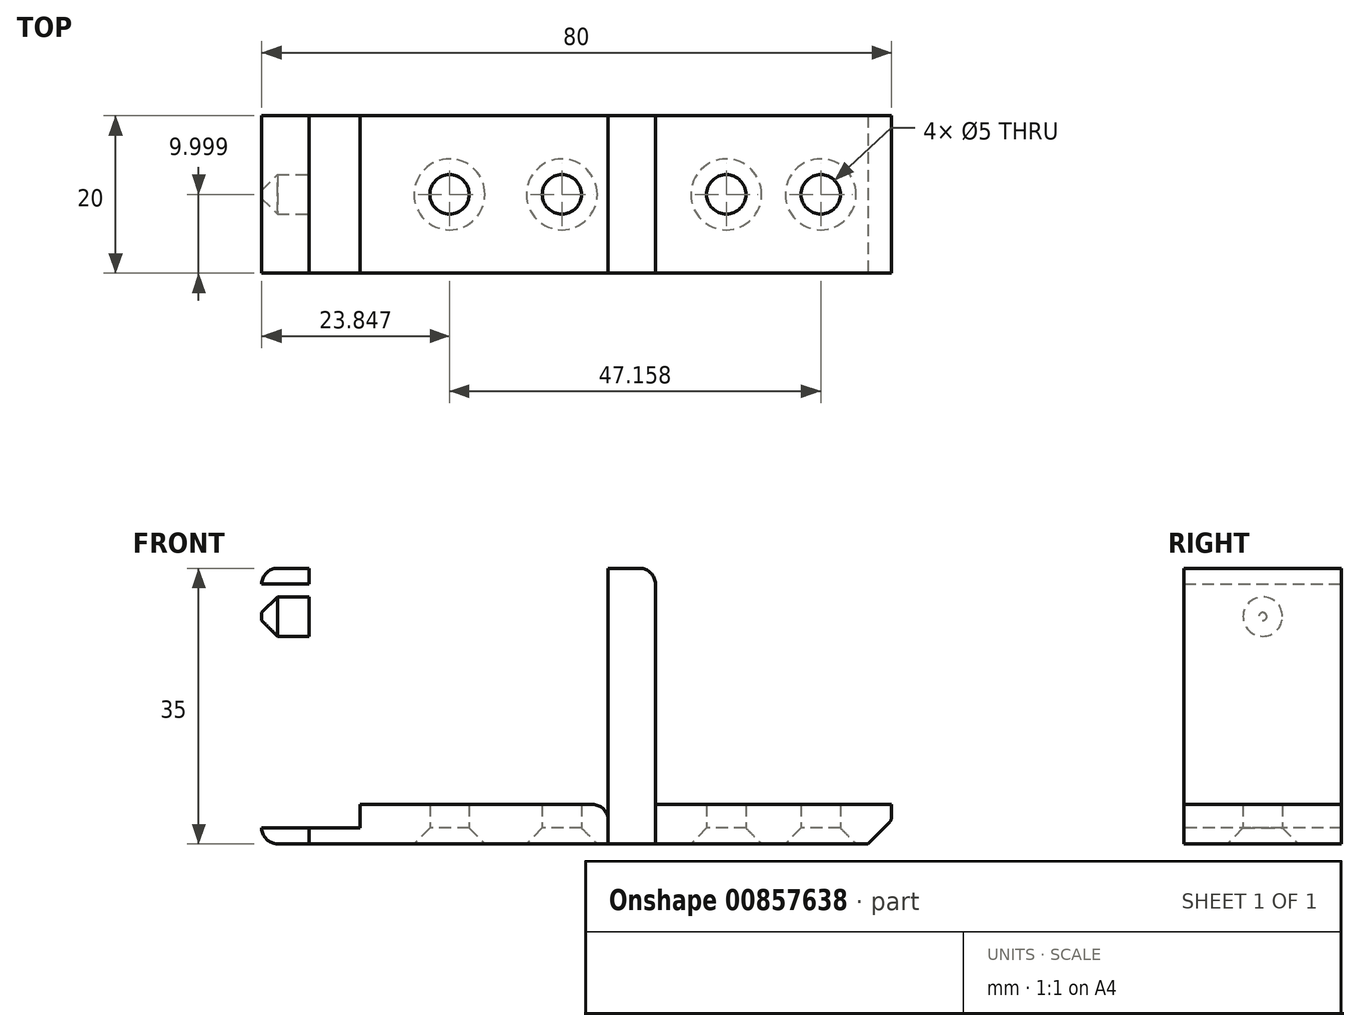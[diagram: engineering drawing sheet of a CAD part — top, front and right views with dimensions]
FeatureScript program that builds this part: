
annotation { "Feature Type Name" : "Feature", "Feature Type Description" : "" }
export const myFeature = defineFeature(function(context is Context, id is Id, definition is map)
    precondition{}
    {
        {
            var Q0;
            Q0=qCreatedBy(makeId("Top.planeOp"),FACE);
            var sketch = newSketch(context, id + "F0", { "sketchPlane" : qUnion([Q0])});
            skLineSegment(sketch, "E0.bottom", {"start": v(-89.34, 30.7) * mm, "end": v(-51.34, 30.7) * mm});
            skLineSegment(sketch, "E0.top", {"start": v(-89.34, 10.7) * mm, "end": v(-51.34, 10.7) * mm});
            skLineSegment(sketch, "E0.left", {"start": v(-89.34, 30.7) * mm, "end": v(-89.34, 10.7) * mm});
            skLineSegment(sketch, "E0.right", {"start": v(-51.34, 30.7) * mm, "end": v(-51.34, 10.7) * mm});
            skLineSegment(sketch, "E1.bottom", {"start": v(-51.34, 30.7) * mm, "end": v(-45.34, 30.7) * mm});
            skLineSegment(sketch, "E1.top", {"start": v(-51.34, 10.7) * mm, "end": v(-45.34, 10.7) * mm});
            skLineSegment(sketch, "E1.right", {"start": v(-45.34, 30.7) * mm, "end": v(-45.34, 10.7) * mm});
            skLineSegment(sketch, "E2.bottom", {"start": v(-89.34, 30.7) * mm, "end": v(-95.34, 30.7) * mm});
            skLineSegment(sketch, "E2.top", {"start": v(-89.34, 10.7) * mm, "end": v(-95.34, 10.7) * mm});
            skLineSegment(sketch, "E2.left", {"start": v(-89.34, 30.7) * mm, "end": v(-89.34, 20.7) * mm});
            skLineSegment(sketch, "E2.right", {"start": v(-95.34, 30.7) * mm, "end": v(-95.34, 10.7) * mm});
            skLineSegment(sketch, "E3.bottom", {"start": v(-45.34, 30.7) * mm, "end": v(-15.34, 30.7) * mm});
            skLineSegment(sketch, "E3.top", {"start": v(-45.34, 10.7) * mm, "end": v(-15.34, 10.7) * mm});
            skLineSegment(sketch, "E3.right", {"start": v(-15.34, 30.7) * mm, "end": v(-15.34, 10.7) * mm});
            skPoint(sketch, "E4", {"position": v(-24.34, 20.7) * mm});
            skPoint(sketch, "E4.positionSnap0", {"position": v(-15.34, 20.7) * mm});
            skPoint(sketch, "E5", {"position": v(-36.34, 20.7) * mm});
            skPoint(sketch, "E5.positionSnap0", {"position": v(-45.34, 20.7) * mm});
            skCircle(sketch, "E6", {"center": v(-36.34, 20.7) * mm, "radius": 2.5 * mm});
            skCircle(sketch, "E7", {"center": v(-24.34, 20.7) * mm, "radius": 2.5 * mm});
            skLineSegment(sketch, "E8", {"start": v(-89.34, 20.7) * mm, "end": v(-89.34, 10.7) * mm});
            skPoint(sketch, "E9.centerSnap0", {"position": v(-70.34, 30.7) * mm});
            skPoint(sketch, "E9.centerSnap1", {"position": v(-89.34, 25.7) * mm});
            skPoint(sketch, "E10.centerSnap0", {"position": v(-89.34, 15.7) * mm});
            skCircle(sketch, "E11", {"center": v(-57.22, 20.7) * mm, "radius": 2.5 * mm});
            skCircle(sketch, "E12", {"center": v(-71.5, 20.7) * mm, "radius": 2.5 * mm});
            skSolve(sketch);
        }
        {
            var Q0;
            Q0=makeQuery(id+"F0.imprint","IMPRINT",FACE,{"disambiguationData":[TD([[makeQuery(id+"F0.imprint","IMPRINT",EDGE,{"derivedFrom":sQuery(id+"F0.wireOp",EDGE,"E2.bottom")}),1.0]])]});
            var Q1;
            Q1=makeQuery(id+"F0.imprint","IMPRINT",FACE,{"disambiguationData":[TD([[makeQuery(id+"F0.imprint","IMPRINT",EDGE,{"derivedFrom":sQuery(id+"F0.wireOp",EDGE,"E1.bottom")}),-1.0]])]});
            extrude(context, id + "F1", {"entities" : qUnion([Q0, Q1]), "depth" : 35 * mm, "offsetDistance" : 25 * mm});
        }
        {
            var Q0;
            Q0=makeQuery(id+"F0.imprint","IMPRINT",FACE,{"disambiguationData":[TD([[makeQuery(id+"F0.imprint","IMPRINT",EDGE,{"derivedFrom":sQuery(id+"F0.wireOp",EDGE,"E0.bottom")}),-1.0]])]});
            var Q1;
            Q1=makeQuery(id+"F0.imprint","IMPRINT",FACE,{"disambiguationData":[TD([[makeQuery(id+"F0.imprint","IMPRINT",EDGE,{"derivedFrom":sQuery(id+"F0.wireOp",EDGE,"E3.bottom")}),-1.0]])]});
            extrude(context, id + "F2", {"entities" : qUnion([Q0, Q1]), "depth" : 5 * mm, "offsetDistance" : 25 * mm});
        }
        {
            var Q0;
            Q0=makeQuery(id+"F2.opExtrude","CAP_EDGE",EDGE,{"disambiguationData":[OSD([sQuery(id+"F0.wireOp",EDGE,"E2.left"),sQuery(id+"F0.wireOp",EDGE,"E8")])],"isStart":false});
            var Q1;
            Q1=makeQuery(id+"F2.opExtrude","CAP_EDGE",EDGE,{"disambiguationData":[OSD([sQuery(id+"F0.wireOp",EDGE,"E0.right")])],"isStart":false});
            var Q2;
            Q2=makeQuery(id+"F1.opExtrude","CAP_EDGE",EDGE,{"disambiguationData":[OSD([sQuery(id+"F0.wireOp",EDGE,"E1.right")])],"isStart":false});
            fillet(context, id + "F3", {"entities" : qUnion([Q0, Q1, Q2]), "radius" : 2 * mm, "tangentPropagation" : true, "allowEdgeOverflow" : false});
        }
        {
            var Q0;
            Q0=makeQuery(id+"F2.opExtrude","CAP_EDGE",EDGE,{"disambiguationData":[OSD([sQuery(id+"F0.wireOp",EDGE,"E3.right")])],"isStart":true});
            chamfer(context, id + "F4", {"entities" : qUnion([Q0]), "width" : 3 * mm, "tangentPropagation" : true});
        }
        {
            var Q0;
            {var subQ0=sQuery(id+"F0.wireOp",EDGE,"E3.right");Q0=makeQuery(id+"F4.opChamfer","BLEND_EDGE",EDGE,{"blendedFrom":[makeQuery(id+"F2.opExtrude","CAP_EDGE",EDGE,{"disambiguationData":[OSD([subQ0])],"isStart":true}),makeQuery(id+"F2.opExtrude","SWEPT_FACE",FACE,{"disambiguationData":[OSD([subQ0])]})],"blendedInto":[makeQuery(id+"F2.opExtrude","SWEPT_FACE",FACE,{"disambiguationData":[OSD([subQ0])]})]});}
            fillet(context, id + "F5", {"entities" : qUnion([Q0]), "radius" : 1 * mm, "tangentPropagation" : true, "allowEdgeOverflow" : false});
        }
        {
            var Q0;
            Q0=makeQuery(id+"F2.opExtrude","CAP_EDGE",EDGE,{"disambiguationData":[OSD([sQuery(id+"F0.wireOp",EDGE,"8xzaLZzM-4nVU-31Vw-sQzU-5eVaGYc0uS2Y")])],"isStart":true});
            var Q1;
            Q1=makeQuery(id+"F2.opExtrude","CAP_EDGE",EDGE,{"disambiguationData":[OSD([sQuery(id+"F0.wireOp",EDGE,"E10")])],"isStart":true});
            var Q2;
            Q2=makeQuery(id+"F2.opExtrude","CAP_EDGE",EDGE,{"disambiguationData":[OSD([sQuery(id+"F0.wireOp",EDGE,"E9")])],"isStart":true});
            var Q3;
            Q3=makeQuery(id+"F2.opExtrude","CAP_EDGE",EDGE,{"disambiguationData":[OSD([sQuery(id+"F0.wireOp",EDGE,"E11")])],"isStart":true});
            var Q4;
            Q4=makeQuery(id+"F2.opExtrude","CAP_EDGE",EDGE,{"disambiguationData":[OSD([sQuery(id+"F0.wireOp",EDGE,"E6")])],"isStart":true});
            var Q5;
            Q5=makeQuery(id+"F2.opExtrude","CAP_EDGE",EDGE,{"disambiguationData":[OSD([sQuery(id+"F0.wireOp",EDGE,"E7")])],"isStart":true});
            var Q6;
            Q6=makeQuery(id+"F2.opExtrude","CAP_EDGE",EDGE,{"disambiguationData":[OSD([sQuery(id+"F0.wireOp",EDGE,"E12")])],"isStart":true});
            chamfer(context, id + "F6", {"entities" : qUnion([Q0, Q1, Q2, Q3, Q4, Q5, Q6]), "width" : 2 * mm, "tangentPropagation" : true});
        }
        {
            var Q0;
            Q0=makeQuery(id+"F1.opExtrude","CAP_EDGE",EDGE,{"disambiguationData":[OSD([sQuery(id+"F0.wireOp",EDGE,"E2.right")])],"isStart":false});
            var Q1;
            Q1=makeQuery(id+"F1.opExtrude","CAP_EDGE",EDGE,{"disambiguationData":[OSD([sQuery(id+"F0.wireOp",EDGE,"E2.right")])],"isStart":true});
            fillet(context, id + "F7", {"entities" : qUnion([Q0, Q1]), "radius" : 2 * mm, "tangentPropagation" : true, "allowEdgeOverflow" : false});
        }
        {
            var Q0;
            Q0=makeQuery(id+"F1.opExtrude","SWEPT_FACE",FACE,{"disambiguationData":[OSD([sQuery(id+"F0.wireOp",EDGE,"E2.right")])]});
            var sketch = newSketch(context, id + "F8", { "sketchPlane" : qUnion([Q0])});
            skLineSegment(sketch, "E13", {"start": v(-20.7, 33) * mm, "end": v(-20.7, 2) * mm});
            skCircle(sketch, "E14", {"center": v(-20.7, 28.87) * mm, "radius": 2.5 * mm});
            skSolve(sketch);
        }
        {
            var Q0;
            {var subQ0=sQuery(id+"F8.wireOp",EDGE,"E14");var subQ1=sQuery(id+"F8.wireOp",EDGE,"E13");var subQ2=makeQuery(id+"F8.imprint","INTERSECT",VERTEX,{"disambiguationData":[OD(0.0)],"derivedFrom":[subQ1,subQ0]});Q0=makeQuery(id+"F8.imprint","IMPRINT",FACE,{"disambiguationData":[TD([[makeQuery(id+"F8.imprint","IMPRINT",EDGE,{"disambiguationData":[TD([[subQ2,-1.0]])],"derivedFrom":subQ1}),1.0]])]});}
            var Q1;
            {var subQ0=sQuery(id+"F8.wireOp",EDGE,"E14");var subQ1=sQuery(id+"F8.wireOp",EDGE,"E13");var subQ2=makeQuery(id+"F8.imprint","INTERSECT",VERTEX,{"disambiguationData":[OD(0.0)],"derivedFrom":[subQ1,subQ0]});Q1=makeQuery(id+"F8.imprint","IMPRINT",FACE,{"disambiguationData":[TD([[makeQuery(id+"F8.imprint","IMPRINT",EDGE,{"disambiguationData":[TD([[subQ2,-1.0]])],"derivedFrom":subQ1}),-1.0]])]});}
            extrude(context, id + "F9", {"entities" : qUnion([Q0, Q1]), "operationType" : NewBodyOperationType.REMOVE, "endBound" : BoundingType.SYMMETRIC, "depth" : 25 * mm, "offsetDistance" : 25 * mm});
        }
        {
            var Q0;
            Q0=makeQuery(id+"F9.boolean.opBoolean","INTERSECT",EDGE,{"derivedFrom":[makeQuery(id+"F1.opExtrude","SWEPT_FACE",FACE,{"disambiguationData":[OSD([sQuery(id+"F0.wireOp",EDGE,"E2.right")])]}),makeQuery(id+"F9.opExtrude","SWEPT_FACE",FACE,{"disambiguationData":[OSD([sQuery(id+"F8.wireOp",EDGE,"E14")])]})]});
            chamfer(context, id + "F10", {"entities" : qUnion([Q0]), "width" : 2 * mm, "tangentPropagation" : true});
        }
    });
